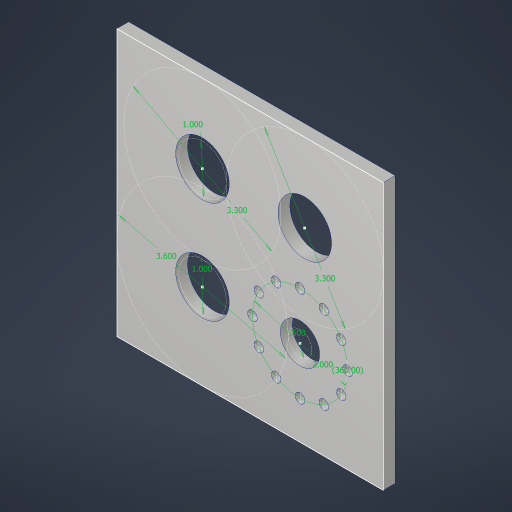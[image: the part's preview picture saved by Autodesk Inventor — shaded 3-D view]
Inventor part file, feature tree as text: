
AUTODESK INVENTOR PART (.ipt)
format: ipt  version: 2023.4 (Build 274418000, 418)  size: 214,528 bytes
history: native  units: in
note: dims shown in document units (in); Inventor stores cm internally (conversion verified against a paired STEP export)
features: hole x3, sketch x1, extrude x1
ambient origin geometry x8: Origin, YZ Plane, XZ Plane, XY Plane, X Axis, Y Axis, Z Axis, Center Point
bodies: Solid1 (feature_tree)
feature tree (5):
  sketch  "Sketch1"  dims[d0=0.5in d1=3.6in d2=1.0in d3=3.3in d4=1.0in d5=3.3in d6=0.25in d7=0.0in d8=1.125in d9=0.38in d10=0.375in d11=0.25in d12=0.5635in d13=1.0in d14=0.8108in d15=2.0in d16=4.7244in d18=360.0deg d20=0.201in d21=0.75in d22=0.385in d23=0.25in d24=0.5635in d25=1.0in d26=0.8108in d27=0.825in d28=0.75in d29=0.375in d30=0.25in d31=0.5635in d32=1.0in d33=0.8108in]
  extrude  "Extrusion1"  Depth=0.25in
  hole  "Hole1"  [1 undecoded]
  hole  "Hole2"  [1 undecoded]
  hole  "Hole3"  [1 undecoded]
note: 3 required parameter values undecoded (feature->parameter linkage not recoverable at this tier; creation-order binding heuristic only, values carry confidence <= 0.55)
